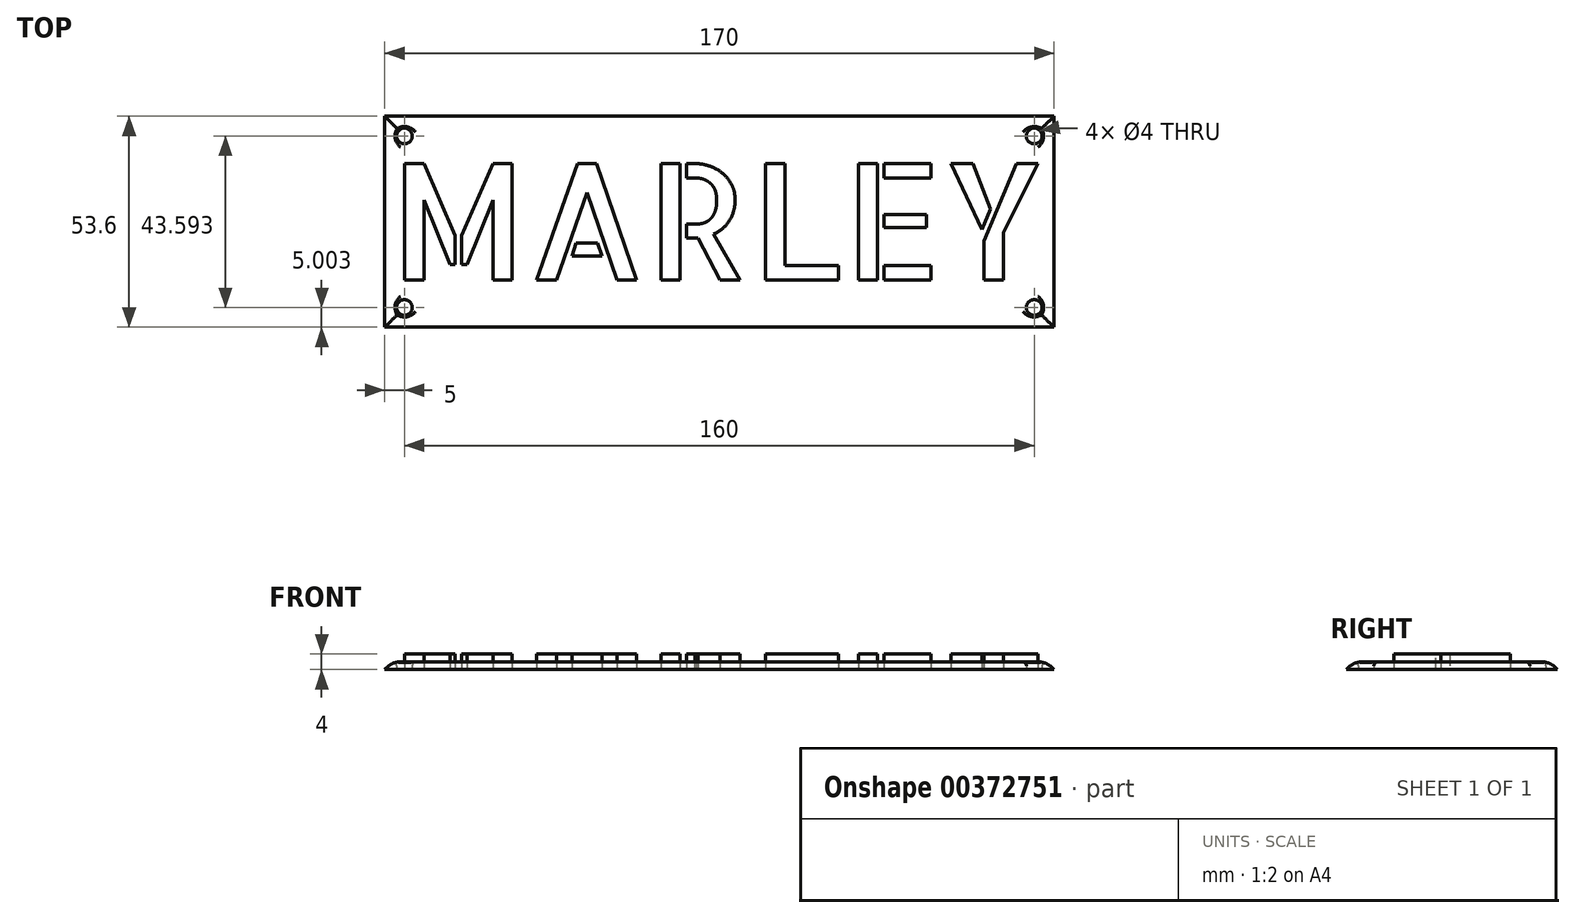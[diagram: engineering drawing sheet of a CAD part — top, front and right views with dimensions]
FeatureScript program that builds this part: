
annotation { "Feature Type Name" : "Feature", "Feature Type Description" : "" }
export const myFeature = defineFeature(function(context is Context, id is Id, definition is map)
    precondition{}
    {
        {
            var Q0;
            Q0=qCreatedBy(makeId("Top.planeOp"),FACE);
            var sketch = newSketch(context, id + "F0", { "sketchPlane" : qUnion([Q0])});
            skLineSegment(sketch, "E0.bottom", {"start": v(85, 26.8) * mm, "end": v(-85, 26.8) * mm});
            skLineSegment(sketch, "E0.top", {"start": v(85, -26.8) * mm, "end": v(-85, -26.8) * mm});
            skLineSegment(sketch, "E0.left", {"start": v(85, 26.8) * mm, "end": v(85, -26.8) * mm});
            skLineSegment(sketch, "E0.right", {"start": v(-85, 26.8) * mm, "end": v(-85, -26.8) * mm});
            skPoint(sketch, "E0.middle", {"position": v(0, 0) * mm});
            skLineSegment(sketch, "E1", {"start": v(0, 89.61) * mm, "end": v(0, -90.19) * mm, "construction": true});
            skSolve(sketch);
        }
        {
            var Q0;
            Q0 = qSketchRegion(id + "F0", true);
            extrude(context, id + "F1", {"entities" : qUnion([Q0]), "depth" : 2 * mm});
        }
        {
            var Q0;
            Q0=qCreatedBy(makeId("Top.planeOp"),FACE);
            var sketch = newSketch(context, id + "F2", { "sketchPlane" : qUnion([Q0])});
            skCircle(sketch, "E2", {"center": v(-80, 21.8) * mm, "radius": 2 * mm});
            skCircle(sketch, "E3", {"center": v(-80, -21.8) * mm, "radius": 2 * mm});
            skCircle(sketch, "E4.MirrorC", {"center": v(80, 21.8) * mm, "radius": 2 * mm});
            skCircle(sketch, "E5.MirrorC", {"center": v(80, -21.8) * mm, "radius": 2 * mm});
            skSolve(sketch);
        }
        {
            var Q0;
            Q0 = qSketchRegion(id + "F2", true);
            extrude(context, id + "F3", {"entities" : qUnion([Q0]), "operationType" : NewBodyOperationType.REMOVE, "endBound" : BoundingType.THROUGH_ALL, "depth" : 25 * mm});
        }
        {
            var Q0;
            Q0=qCreatedBy(makeId("Top.planeOp"),FACE);
            var sketch = newSketch(context, id + "F4", { "sketchPlane" : qUnion([Q0])});
            skText(sketch, "E6", { "text": "MARLEY", "fontName": "AllertaStencil-Regular.ttf"});
            skLineSegment(sketch, "E7.0", {"start": v(0, 89.61) * mm, "end": v(0, -90.19) * mm, "construction": true});
            const initialGuessF4  = {"E6": [-0.08364, -0.0148, 1, 0, 0.0296]};
            skSetInitialGuess(sketch, initialGuessF4);
            skSolve(sketch);
        }
        {
            var Q0;
            Q0 = qSketchRegion(id + "F4", true);
            extrude(context, id + "F5", {"entities" : qUnion([Q0]), "depth" : 4 * mm});
        }
        {
            var Q0;
            Q0=makeQuery(id+"F3.boolean.opBoolean","INTERSECT",EDGE,{"derivedFrom":[makeQuery(id+"F1.opExtrude","CAP_FACE",FACE,{"disambiguationData":[OSD([sQuery(id+"F0.wireOp",EDGE,"E0.bottom"),sQuery(id+"F0.wireOp",EDGE,"E0.top"),sQuery(id+"F0.wireOp",EDGE,"E0.left"),sQuery(id+"F0.wireOp",EDGE,"E0.right")])],"isStart":false}),makeQuery(id+"F3.opExtrude","SWEPT_FACE",FACE,{"disambiguationData":[OSD([sQuery(id+"F2.wireOp",EDGE,"E2")])]})]});
            var Q1;
            Q1=makeQuery(id+"F3.boolean.opBoolean","INTERSECT",EDGE,{"derivedFrom":[makeQuery(id+"F1.opExtrude","CAP_FACE",FACE,{"disambiguationData":[OSD([sQuery(id+"F0.wireOp",EDGE,"E0.bottom"),sQuery(id+"F0.wireOp",EDGE,"E0.top"),sQuery(id+"F0.wireOp",EDGE,"E0.left"),sQuery(id+"F0.wireOp",EDGE,"E0.right")])],"isStart":false}),makeQuery(id+"F3.opExtrude","SWEPT_FACE",FACE,{"disambiguationData":[OSD([sQuery(id+"F2.wireOp",EDGE,"E3")])]})]});
            var Q2;
            Q2=makeQuery(id+"F3.boolean.opBoolean","INTERSECT",EDGE,{"derivedFrom":[makeQuery(id+"F1.opExtrude","CAP_FACE",FACE,{"disambiguationData":[OSD([sQuery(id+"F0.wireOp",EDGE,"E0.bottom"),sQuery(id+"F0.wireOp",EDGE,"E0.top"),sQuery(id+"F0.wireOp",EDGE,"E0.left"),sQuery(id+"F0.wireOp",EDGE,"E0.right")])],"isStart":false}),makeQuery(id+"F3.opExtrude","SWEPT_FACE",FACE,{"disambiguationData":[OSD([sQuery(id+"F2.wireOp",EDGE,"E5.MirrorC")])]})]});
            var Q3;
            Q3=makeQuery(id+"F3.boolean.opBoolean","INTERSECT",EDGE,{"derivedFrom":[makeQuery(id+"F1.opExtrude","CAP_FACE",FACE,{"disambiguationData":[OSD([sQuery(id+"F0.wireOp",EDGE,"E0.bottom"),sQuery(id+"F0.wireOp",EDGE,"E0.top"),sQuery(id+"F0.wireOp",EDGE,"E0.left"),sQuery(id+"F0.wireOp",EDGE,"E0.right")])],"isStart":false}),makeQuery(id+"F3.opExtrude","SWEPT_FACE",FACE,{"disambiguationData":[OSD([sQuery(id+"F2.wireOp",EDGE,"E4.MirrorC")])]})]});
            fillet(context, id + "F6", {"entities" : qUnion([Q0, Q1, Q2, Q3]), "radius" : 1 * mm, "tangentPropagation" : true, "allowEdgeOverflow" : false});
        }
        {
            var Q0;
            Q0=makeQuery(id+"F1.opExtrude","CAP_EDGE",EDGE,{"disambiguationData":[OSD([sQuery(id+"F0.wireOp",EDGE,"E0.top")])],"isStart":false});
            var Q1;
            Q1=makeQuery(id+"F1.opExtrude","CAP_EDGE",EDGE,{"disambiguationData":[OSD([sQuery(id+"F0.wireOp",EDGE,"E0.right")])],"isStart":false});
            var Q2;
            Q2=makeQuery(id+"F1.opExtrude","CAP_EDGE",EDGE,{"disambiguationData":[OSD([sQuery(id+"F0.wireOp",EDGE,"E0.left")])],"isStart":false});
            var Q3;
            Q3=makeQuery(id+"F1.opExtrude","CAP_EDGE",EDGE,{"disambiguationData":[OSD([sQuery(id+"F0.wireOp",EDGE,"E0.bottom")])],"isStart":false});
            fillet(context, id + "F7", {"entities" : qUnion([Q0, Q1, Q2, Q3]), "radius" : 5 * mm, "tangentPropagation" : true, "allowEdgeOverflow" : false});
        }
    });
